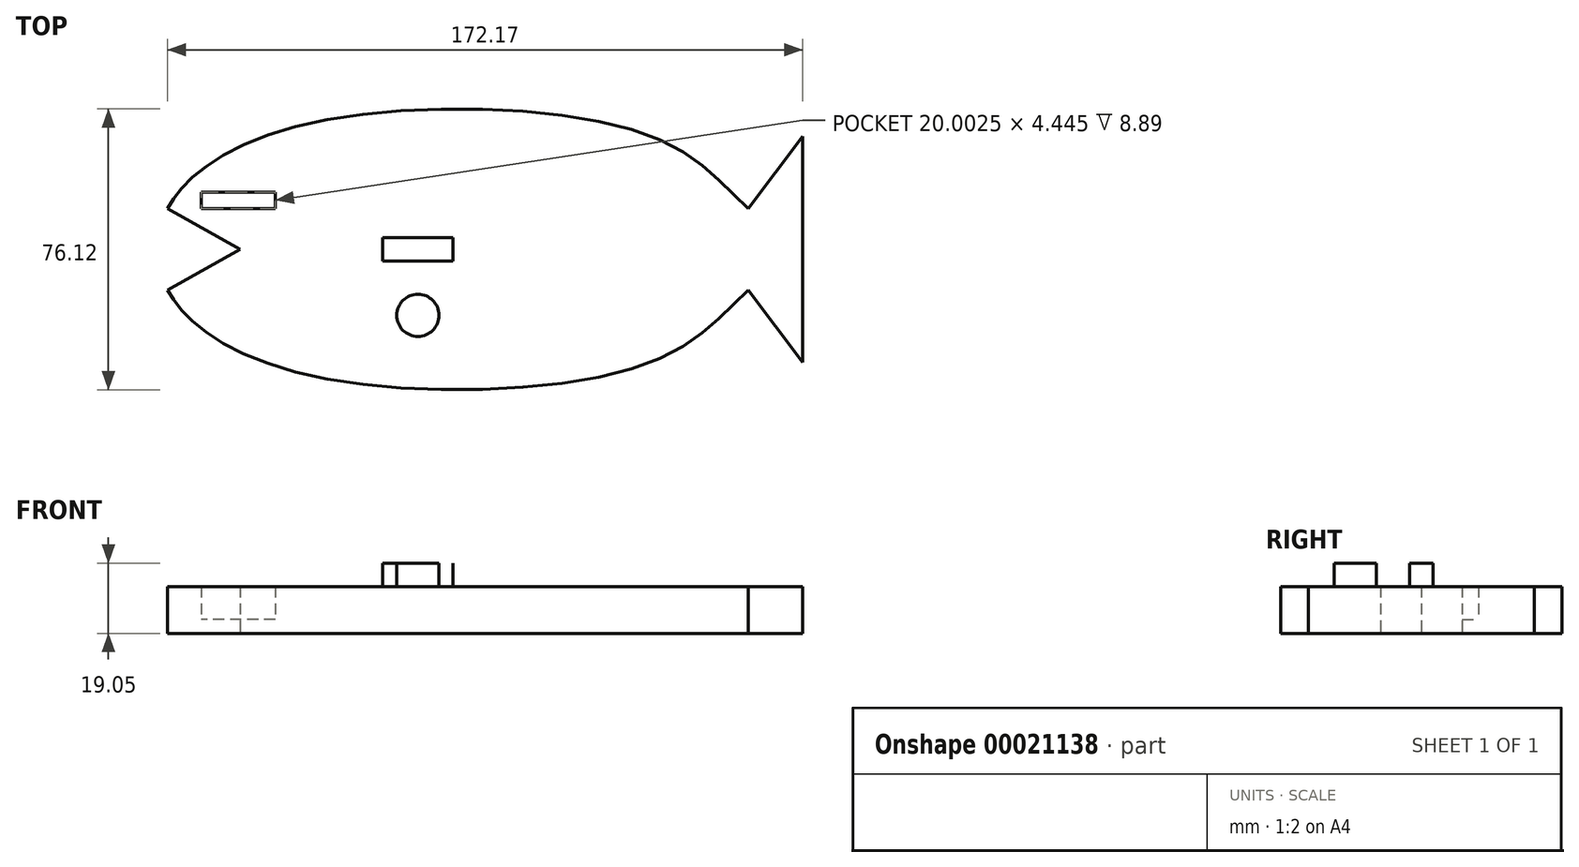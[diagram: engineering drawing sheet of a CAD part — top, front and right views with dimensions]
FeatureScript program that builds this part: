
annotation { "Feature Type Name" : "Feature", "Feature Type Description" : "" }
export const myFeature = defineFeature(function(context is Context, id is Id, definition is map)
    precondition{}
    {
        {
            var Q0;
            Q0=qCreatedBy(makeId("Top.planeOp"),FACE);
            var sketch = newSketch(context, id + "F0", { "sketchPlane" : qUnion([Q0])});
            skFitSpline(sketch, "E0", {"points": [v(89.47, 28.98) * mm, v(63.18, 48.55) * mm, v(-25.37, 52.9) * mm, v(-60.56, 37.87) * mm, v(-67.87, 28.98) * mm], "startDerivative": vector(-90.55, 84.73) * mm, "endDerivative": vector(-33.24, -55.1) * mm});
            skLineSegment(sketch, "E1", {"start": v(-67.87, 28.98) * mm, "end": v(-48.1, 17.9) * mm});
            skLineSegment(sketch, "E2", {"start": v(-48.1, 17.9) * mm, "end": v(104.3, 17.9) * mm, "construction": true});
            skLineSegment(sketch, "E3", {"start": v(89.47, 28.98) * mm, "end": v(104.3, 48.55) * mm});
            skLineSegment(sketch, "E4", {"start": v(104.3, 48.55) * mm, "end": v(104.3, 17.9) * mm});
            skLineSegment(sketch, "E5.MirrorCS", {"start": v(-67.87, 6.84) * mm, "end": v(-48.1, 17.9) * mm});
            skFitSpline(sketch, "E6.MirrorCS", {"points": [v(89.47, 6.84) * mm, v(63.18, -12.73) * mm, v(-25.37, -17.08) * mm, v(-60.56, -2.06) * mm, v(-67.87, 6.84) * mm], "startDerivative": vector(-90.55, -84.73) * mm, "endDerivative": vector(-33.24, 55.1) * mm});
            skLineSegment(sketch, "E7.MirrorCS", {"start": v(89.47, 6.84) * mm, "end": v(104.3, -12.73) * mm});
            skLineSegment(sketch, "E8.MirrorCS", {"start": v(104.3, -12.73) * mm, "end": v(104.3, 17.9) * mm});
            skLineSegment(sketch, "E9.rect.bottom", {"start": v(-38.66, 28.98) * mm, "end": v(-58.67, 28.98) * mm});
            skLineSegment(sketch, "E9.rect.top", {"start": v(-38.66, 33.42) * mm, "end": v(-58.67, 33.42) * mm});
            skLineSegment(sketch, "E9.rect.left", {"start": v(-38.66, 28.98) * mm, "end": v(-38.66, 33.42) * mm});
            skLineSegment(sketch, "E9.rect.right", {"start": v(-58.67, 28.98) * mm, "end": v(-58.67, 33.42) * mm});
            skPoint(sketch, "E9.rect.middle", {"position": v(-48.67, 31.2) * mm});
            skSolve(sketch);
        }
        {
            var Q0;
            {var subQ1=sQuery(id+"F0.wireOp",EDGE,"E5.MirrorCS");Q0=makeQuery(id+"F0.imprint","IMPRINT",FACE,{"disambiguationData":[TD([[makeQuery(id+"F0.imprint","IMPRINT",EDGE,{"derivedFrom":subQ1}),-1.0]])]});}
            var Q1;
            Q1=makeQuery(id+"F0.imprint","IMPRINT",FACE,{"disambiguationData":[TD([[makeQuery(id+"F0.imprint","IMPRINT",EDGE,{"derivedFrom":sQuery(id+"F0.wireOp",EDGE,"E0")}),1.0]])]});
            extrude(context, id + "F1", {"entities" : qUnion([Q0, Q1]), "depth" : 12.7 * mm});
        }
        {
            var Q0;
            Q0=qCreatedBy(makeId("Top.planeOp"),FACE);
            var sketch = newSketch(context, id + "F2", { "sketchPlane" : qUnion([Q0])});
            skCircle(sketch, "E10", {"center": v(0, 0) * mm, "radius": 5.72 * mm});
            skSolve(sketch);
        }
        {
            var Q0;
            Q0 = qSketchRegion(id + "F2", true);
            extrude(context, id + "F3", {"entities" : qUnion([Q0]), "operationType" : NewBodyOperationType.ADD, "depth" : 19.05 * mm});
        }
        {
            var Q0;
            Q0=qCreatedBy(makeId("Top.planeOp"),FACE);
            var sketch = newSketch(context, id + "F4", { "sketchPlane" : qUnion([Q0])});
            skLineSegment(sketch, "E11.rect.bottom", {"start": v(9.53, 21.1) * mm, "end": v(-9.53, 21.1) * mm});
            skLineSegment(sketch, "E11.rect.top", {"start": v(9.53, 14.76) * mm, "end": v(-9.53, 14.76) * mm});
            skLineSegment(sketch, "E11.rect.left", {"start": v(9.53, 21.1) * mm, "end": v(9.53, 14.76) * mm});
            skLineSegment(sketch, "E11.rect.right", {"start": v(-9.53, 21.1) * mm, "end": v(-9.53, 14.76) * mm});
            skPoint(sketch, "E11.rect.middle", {"position": v(0, 17.93) * mm});
            skSolve(sketch);
        }
        {
            var Q0;
            Q0 = qSketchRegion(id + "F4", true);
            extrude(context, id + "F5", {"entities" : qUnion([Q0]), "operationType" : NewBodyOperationType.ADD, "depth" : 19.05 * mm});
        }
        {
            var Q0;
            Q0=makeQuery(id+"F0.imprint","IMPRINT",FACE,{"disambiguationData":[TD([[makeQuery(id+"F0.imprint","IMPRINT",EDGE,{"derivedFrom":sQuery(id+"F0.wireOp",EDGE,"E9.rect.bottom")}),-1.0]])]});
            extrude(context, id + "F6", {"entities" : qUnion([Q0]), "operationType" : NewBodyOperationType.ADD, "depth" : 3.8 * mm});
        }
    });
